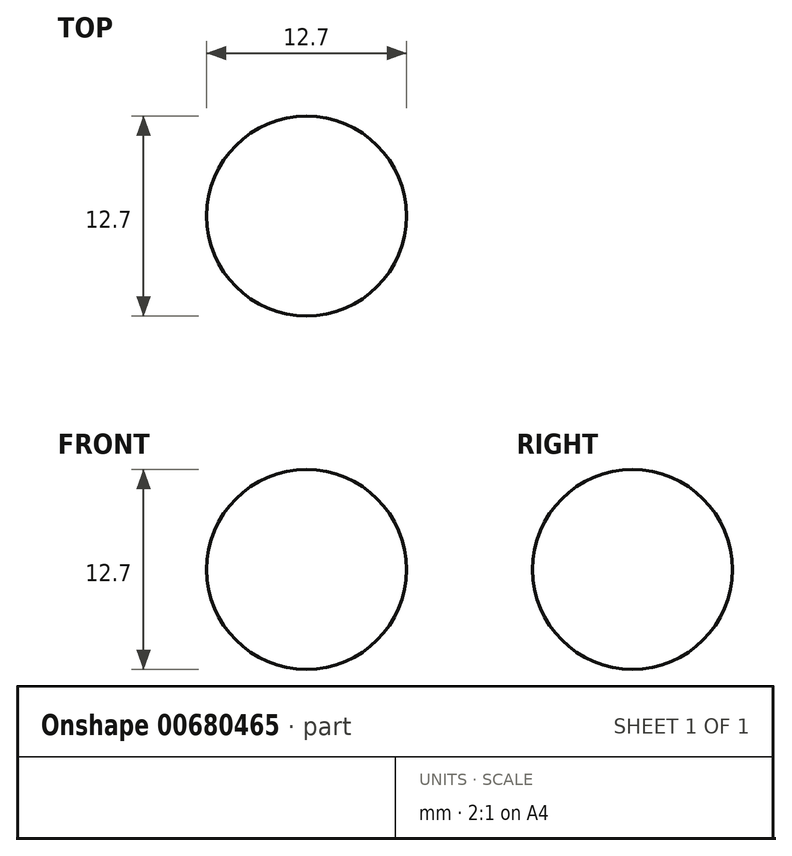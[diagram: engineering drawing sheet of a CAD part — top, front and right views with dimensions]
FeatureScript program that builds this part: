
annotation { "Feature Type Name" : "Feature", "Feature Type Description" : "" }
export const myFeature = defineFeature(function(context is Context, id is Id, definition is map)
    precondition{}
    {
        {
            var Q0;
            Q0=qCreatedBy(makeId("Front.planeOp"),FACE);
            var sketch = newSketch(context, id + "F0", { "sketchPlane" : qUnion([Q0])});
            skArc(sketch, "E0", {"start": v(0, -6.35) * mm, "mid": v(6.35, 0) * mm, "end": v(0, 6.35) * mm});
            skLineSegment(sketch, "E1", {"start": v(0, 6.35) * mm, "end": v(0, -6.35) * mm});
            skSolve(sketch);
        }
        {
            var Q0;
            Q0=qCreatedBy(makeId("Front.planeOp"),FACE);
            var sketch = newSketch(context, id + "F1", { "sketchPlane" : qUnion([Q0])});
            skLineSegment(sketch, "E2", {"start": v(0, 41.86) * mm, "end": v(0, -38.97) * mm});
            skSolve(sketch);
        }
        {
            var Q0;
            Q0=makeQuery(id+"F0.imprint","IMPRINT",FACE,{"disambiguationData":[TD([[makeQuery(id+"F0.imprint","IMPRINT",EDGE,{"derivedFrom":sQuery(id+"F0.wireOp",EDGE,"E0")}),1.0]])]});
            var Q1;
            Q1=sQuery(id+"F1.wireOp",EDGE,"E2");
            revolve(context, id + "F2", {"entities" : qUnion([Q0]), "axis" : qUnion([Q1]), "revolveType" : RevolveType.FULL});
        }
    });
